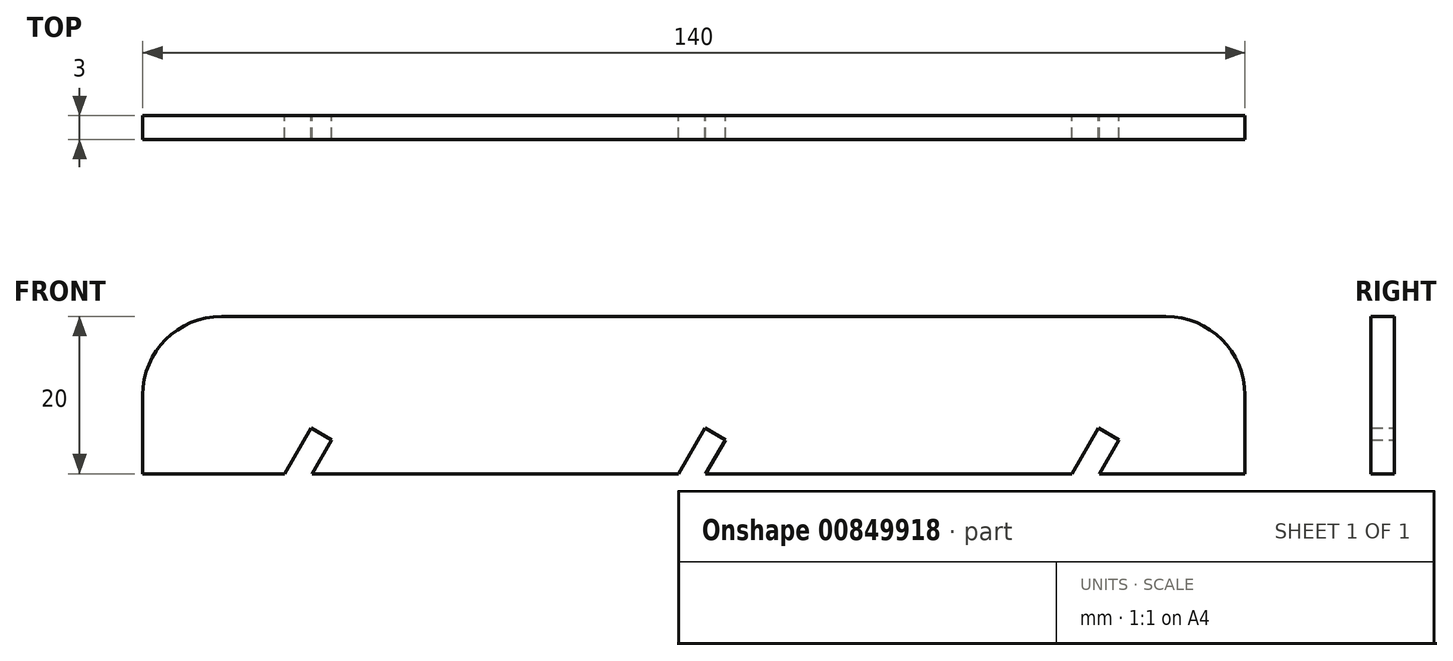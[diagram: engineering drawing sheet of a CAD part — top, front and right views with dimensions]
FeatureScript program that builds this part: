
annotation { "Feature Type Name" : "Feature", "Feature Type Description" : "" }
export const myFeature = defineFeature(function(context is Context, id is Id, definition is map)
    precondition{}
    {
        {
            var Q0;
            Q0=qCreatedBy(makeId("Front.planeOp"),FACE);
            var sketch = newSketch(context, id + "F0", { "sketchPlane" : qUnion([Q0])});
            skLineSegment(sketch, "E0.bottom", {"start": v(-70, -10) * mm, "end": v(70, -10) * mm});
            skPoint(sketch, "E0.middle", {"position": v(0, 0) * mm});
            skLineSegment(sketch, "E1", {"start": v(-70, -10) * mm, "end": v(-70, 0) * mm});
            skLineSegment(sketch, "E2", {"start": v(70, -10) * mm, "end": v(70, 0) * mm});
            skLineSegment(sketch, "E3", {"start": v(-60, 10) * mm, "end": v(60, 10) * mm});
            skArc(sketch, "E4", {"start": v(-60, 10) * mm, "mid": v(-67.07, 7.07) * mm, "end": v(-70, 0) * mm});
            skArc(sketch, "E5", {"start": v(70, 0) * mm, "mid": v(67.07, 7.07) * mm, "end": v(60, 10) * mm});
            skLineSegment(sketch, "E6", {"start": v(-70, -10) * mm, "end": v(-50, -10) * mm});
            skLineSegment(sketch, "E7", {"start": v(-50, -10) * mm, "end": v(0, -10) * mm});
            skLineSegment(sketch, "E8", {"start": v(0, -10) * mm, "end": v(50, -10) * mm});
            skLineSegment(sketch, "E9", {"start": v(50, -10) * mm, "end": v(70, -10) * mm});
            skLineSegment(sketch, "E10", {"start": v(-50, -10) * mm, "end": v(-51.5, -10) * mm});
            skLineSegment(sketch, "E11", {"start": v(-51.5, -10) * mm, "end": v(-48.5, -10) * mm});
            skLineSegment(sketch, "E12", {"start": v(-48.5, -10) * mm, "end": v(-46, -5.67) * mm});
            skLineSegment(sketch, "E13", {"start": v(-46, -5.67) * mm, "end": v(-48.6, -4.17) * mm});
            skLineSegment(sketch, "E14", {"start": v(-48.6, -4.17) * mm, "end": v(-51.96, -10) * mm});
            skLineSegment(sketch, "E15", {"start": v(0, -10) * mm, "end": v(1.5, -10) * mm});
            skLineSegment(sketch, "E16", {"start": v(1.5, -10) * mm, "end": v(4, -5.67) * mm});
            skLineSegment(sketch, "E17", {"start": v(4, -5.67) * mm, "end": v(1.4, -4.17) * mm});
            skLineSegment(sketch, "E18", {"start": v(1.4, -4.17) * mm, "end": v(-1.96, -10) * mm});
            skLineSegment(sketch, "E19", {"start": v(50, -10) * mm, "end": v(51.5, -10) * mm});
            skLineSegment(sketch, "E20", {"start": v(51.5, -10) * mm, "end": v(54, -5.67) * mm});
            skLineSegment(sketch, "E21", {"start": v(54, -5.67) * mm, "end": v(51.4, -4.17) * mm});
            skLineSegment(sketch, "E22", {"start": v(51.4, -4.17) * mm, "end": v(48.04, -10) * mm});
            skSolve(sketch);
        }
        {
            var Q0;
            {var subQ7=sQuery(id+"F0.wireOp",EDGE,"E1");Q0=makeQuery(id+"F0.imprint","IMPRINT",FACE,{"disambiguationData":[TD([[makeQuery(id+"F0.imprint","IMPRINT",EDGE,{"derivedFrom":subQ7}),-1.0]])]});}
            extrude(context, id + "F1", {"entities" : qUnion([Q0]), "depth" : 3 * mm, "offsetDistance" : 25 * mm});
        }
    });
